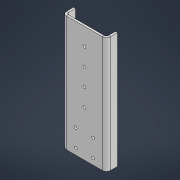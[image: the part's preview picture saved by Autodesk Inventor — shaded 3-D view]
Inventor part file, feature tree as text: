
AUTODESK INVENTOR PART (.ipt)
format: ipt  version: 2022 (Build 260153000, 153)  size: 179,712 bytes
history: native  units: in
note: dims shown in document units (in); Inventor stores cm internally (conversion verified against a paired STEP export)
features: sheet_metal_op x4, other x3, sketch x2, hole x1
ambient origin geometry x8: Origin, YZ Plane, XZ Plane, XY Plane, X Axis, Y Axis, Z Axis, Center Point
bodies: Solid2 (feature_tree)
feature tree (10):
  sketch  "Sketch1"  dims[d0=0.7874in d1=0.7874in]
  sheet_metal_op  "Face1"
  hole  "Hole1"  [1 undecoded]
  sheet_metal_op  "Flange1"
  other  "Plate1"
  sketch  "Sketch2"  dims[d2=0.9843in d3=0.7874in d4=0.2756in d5=0.5906in d6=0.09in d7=0.1339in d8=0.2362in d9=0.2559in d10=0.1181in d11=0.6181in d12=0.09in d13=0.8108in d14=0.09in d15=0.045in d16=0.18in d17=0.09in d18=0.5in d19=90.0deg d20=0.09in d21=0.36in d22=0.09in d23=0.09in]
  other  "Plate2"
  sheet_metal_op  "Bend1"
  sheet_metal_op  "Corner1"
  other  "Definition1"
note: 1 required parameter value undecoded (feature->parameter linkage not recoverable at this tier; creation-order binding heuristic only, values carry confidence <= 0.55)
